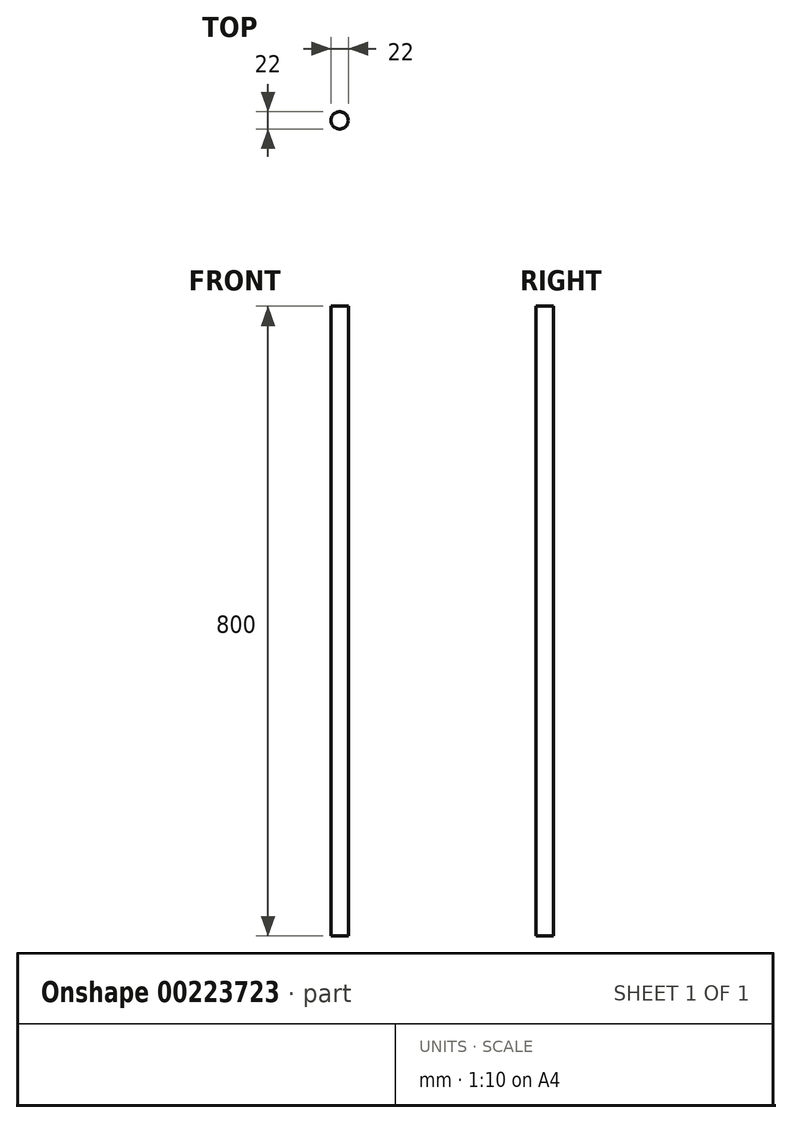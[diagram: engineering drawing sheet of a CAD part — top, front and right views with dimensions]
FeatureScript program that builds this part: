
annotation { "Feature Type Name" : "Feature", "Feature Type Description" : "" }
export const myFeature = defineFeature(function(context is Context, id is Id, definition is map)
    precondition{}
    {
        {
            var Q0;
            Q0=qCreatedBy(makeId("Top.planeOp"),FACE);
            var sketch = newSketch(context, id + "F0", { "sketchPlane" : qUnion([Q0])});
            skCircle(sketch, "E0", {"center": v(0, 0) * mm, "radius": 11 * mm});
            skSolve(sketch);
        }
        {
            var Q0;
            Q0=makeQuery(id+"F0.imprint","IMPRINT",FACE,{"disambiguationData":[TD([[makeQuery(id+"F0.imprint","IMPRINT",EDGE,{"derivedFrom":sQuery(id+"F0.wireOp",EDGE,"E0")}),1.0]])]});
            extrude(context, id + "F1", {"entities" : qUnion([Q0]), "depth" : 800 * mm});
        }
    });
